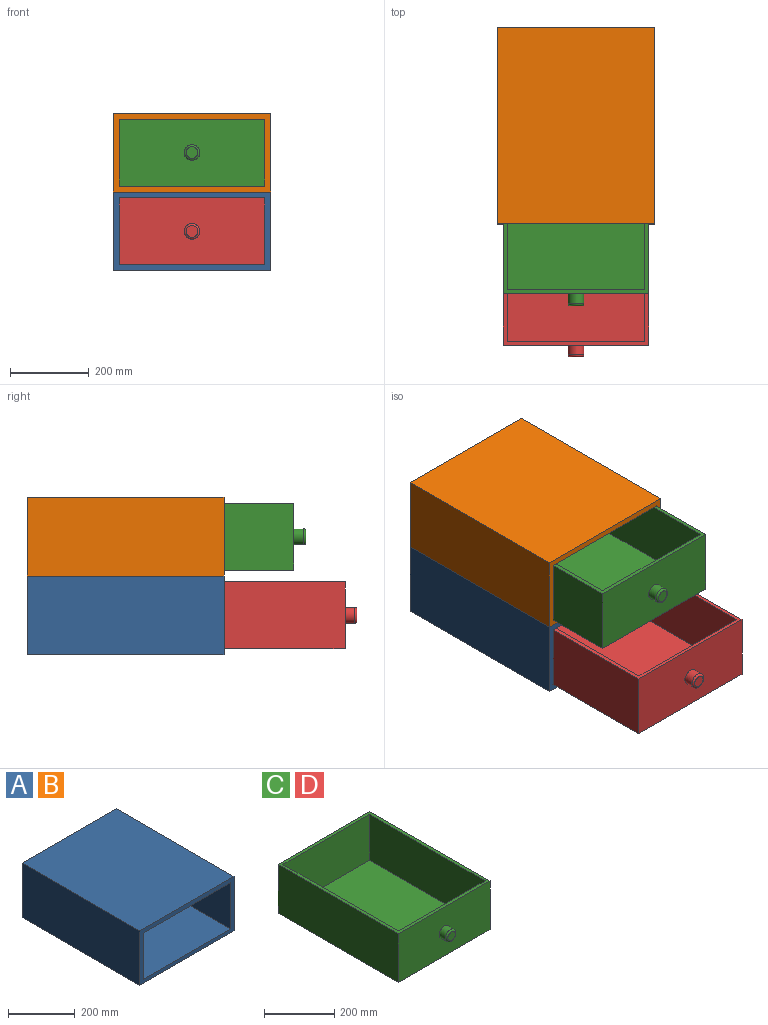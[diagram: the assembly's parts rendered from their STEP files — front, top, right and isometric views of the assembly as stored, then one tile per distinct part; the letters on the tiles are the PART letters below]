
ASSEMBLY  parts=4 mates=3
PART A: 11 faces, bbox 400x500x200 mm
  f0: plane 400x200mm, normal (0,-1,0), area 17100mm2, adj f1,f2,f3,f4,f6,f7,f8,f9
  f1: plane 500x200mm, normal (1,0,0), area 100000mm2, adj f0,f2,f4,f5
  f2: plane 500x400mm, normal (0,0,1), area 200000mm2, adj f0,f1,f3,f5
  f3: plane 500x200mm, normal (-1,0,0), area 100000mm2, adj f0,f2,f4,f5
  f4: plane 500x400mm, normal (0,0,-1), area 200000mm2, adj f0,f1,f3,f5
  f5: plane 400x200mm, normal (0,1,0), area 80000mm2, adj f1,f2,f3,f4
  f6: plane 485x170mm, normal (-1,0,0), area 82450mm2, adj f0,f7,f9,f10
  f7: plane 485x370mm, normal (0,0,-1), area 179450mm2, adj f0,f6,f8,f10
  f8: plane 485x170mm, normal (1,0,0), area 82450mm2, adj f0,f7,f9,f10
  f9: plane 485x370mm, normal (0,0,1), area 179450mm2, adj f0,f6,f8,f10
  f10: plane 370x170mm, normal (0,-1,0), area 62900mm2, adj f6,f7,f8,f9
PART B: same geometry as A
PART C: 16 faces, bbox 370x515x170 mm
  f0: plane 485x370mm, normal (0,0,1), area 16700mm2, adj f1,f2,f4,f5,f9,f10,f12,f13
  f1: plane 485x170mm, normal (1,0,0), area 82450mm2, adj f0,f3,f4,f5
  f2: plane 485x170mm, normal (-1,0,0), area 82450mm2, adj f0,f3,f4,f5
  f3: plane 485x370mm, normal (0,0,-1), area 179450mm2, adj f1,f2,f4,f5
  f4: plane 370x170mm, normal (0,-1,0), area 61643.4mm2, adj f0,f1,f2,f3,f6
  f5: plane 370x170mm, normal (0,1,0), area 62900mm2, adj f0,f1,f2,f3
  f6: cylinder r=20mm len=40mm, axis (0,1,0), area 3141.6mm2, adj f4,f8
  f7: plane 30x30mm, normal (0,-1,0), area 706.9mm2, adj f8
  f8: torus R=15mm, axis (0,-1,0), area 897.3mm2, adj f6,f7
  f9: plane 465x160mm, normal (-1,0,0), area 74400mm2, adj f0,f11,f12,f13
  f10: plane 465x160mm, normal (1,0,0), area 74400mm2, adj f0,f11,f12,f13
  f11: plane 465x350mm, normal (0,0,1), area 162750mm2, adj f9,f10,f12,f13
  f12: plane 350x160mm, normal (0,1,0), area 55685.8mm2, adj f0,f9,f10,f11,f14
  f13: plane 350x160mm, normal (0,-1,0), area 56000mm2, adj f0,f9,f10,f11
  f14: cylinder r=10mm len=30mm, axis (0,1,0), area 1885mm2, adj f12,f15
  f15: plane 20x20mm, normal (0,1,0), area 314.2mm2, adj f14
PART D: same geometry as C
PLACE A at identity fixed
PLACE B t=(0,0,200)mm
PLACE C t=(0,-177.56,200)mm
PLACE D t=(0,-307.44,0)mm
MATE slider A.f10 <-> D.f5  axis (0,-1,0) through (-185,235,-85)mm
MATE slider B.f0 <-> C.f5  axis (0,1,0) through (-185,-250,115)mm
MATE fastened B.f1 <-> A.f1  axis (1,0,0) through (200,250,100)mm
